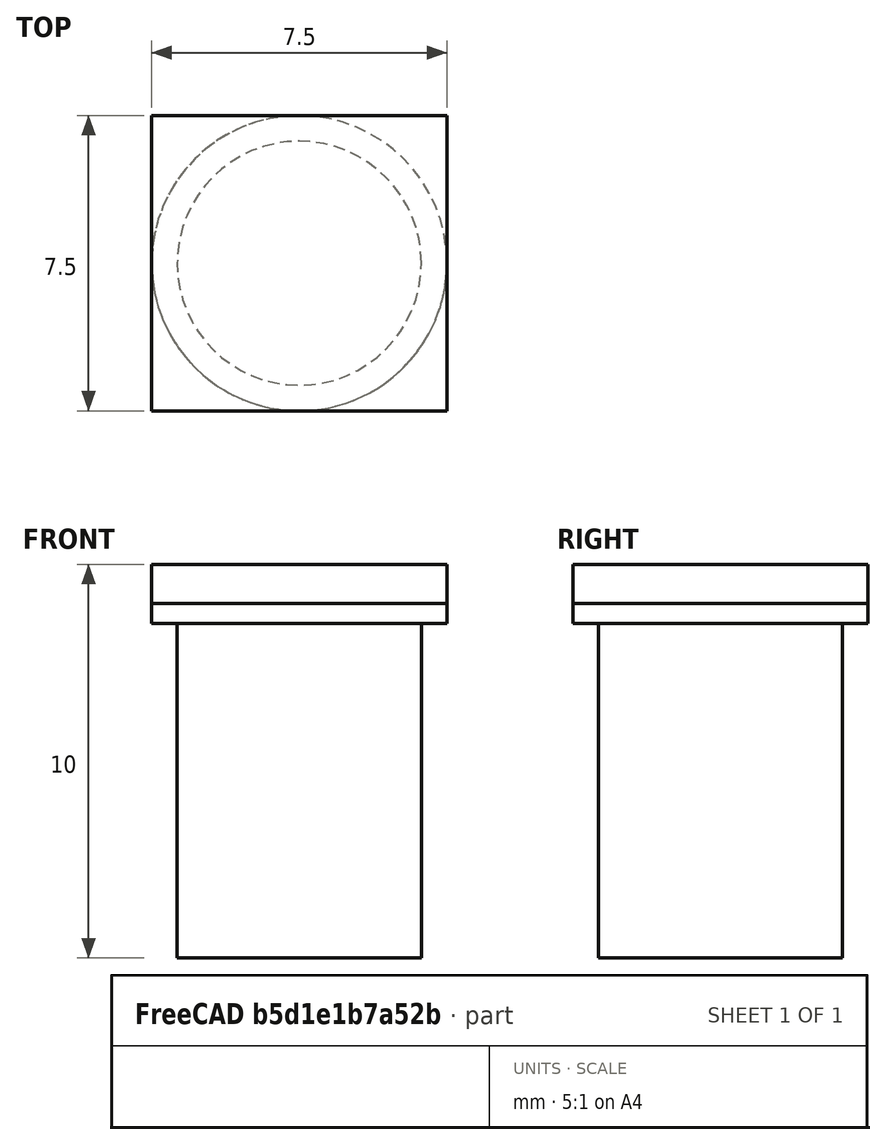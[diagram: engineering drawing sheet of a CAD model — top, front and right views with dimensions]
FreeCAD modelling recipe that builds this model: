
FCSTD DOCUMENT  (FreeCAD 0.17R13522 (Git))
Label: perforador_led_5mmVerdadero
License: CreativeCommons Attribution-ShareAlike
LicenseURL: http://creativecommons.org/licenses/by-sa/4.0/
objects: Part::Part2DObjectPython×2, Part::Extrusion×2, Part::Fuse×2, Part::Box×1
note: 7 computed .brp shape members not serialized (recipe doc carries the construction recipe); baked Part::Feature solids carry a one-line shape summary decoded from their .brp

FEATURE [Part::Box] Box  label="base"
  AttacherType = Attacher::AttachEngine3D
  Height = 1
  Length = 7.5
  Width = 7.5
FEATURE [Part::Part2DObjectPython] Circle  label="circulo exterior diametro 7.5"  # Draft 2D object (typed FeaturePython)
  FirstAngle = 0
  LastAngle = 0
  MakeFace = true
  Placement = pos=(3.75,3.75,1) rot=(0,0,1;3.14159rad)
  Radius = 3.75
FEATURE [Part::Part2DObjectPython] Circle001  label="circulo inerior diametro 6.2"  # Draft 2D object (typed FeaturePython)
  FirstAngle = 0
  LastAngle = 0
  MakeFace = true
  Placement = pos=(3.75,3.75,1) rot=(0,0,1;3.14159rad)
  Radius = 3.1
FEATURE [Part::Extrusion] Extrude  label="Extrude interior pasante"
  Base = -> Circle001
  Dir = (0,0,1)
  DirMode = 2
  FaceMakerClass = Part::FaceMakerBullseye
  LengthFwd = 10
  LengthRev = 0
  Placement = pos=(0,0,-10) rot=(0,0,1;0rad)
  Solid = false
  Symmetric = false
FEATURE [Part::Extrusion] Extrude001  label="Extrude001 perfora 0.5"
  Base = -> Circle
  Dir = (0,0,1)
  DirMode = 2
  FaceMakerClass = Part::FaceMakerBullseye
  LengthFwd = 1.5
  LengthRev = 0
  Placement = pos=(0,0,-1.5) rot=(0,0,1;0rad)
  Solid = false
  Symmetric = false
FEATURE [Part::Fuse] Fusion
  Base = -> Extrude
  Refine = true
  Tool = -> Extrude001
FEATURE [Part::Fuse] Fusion001  label="perforador led 5 mm"
  Base = -> Box
  Refine = true
  Tool = -> Fusion
